# Revit family: Bath_Combination-GROHE-Concetto-19576_Series
name_source: partatom
category: Plumbing Fixtures
revit_build: Autodesk Revit 2014 (Build: 20130308_1515(x64)
units: mm (PartAtom-declared; Revit-internal decimal feet)

## types (2) — shared parameters
ADA Compliant = Yes
CW Connection = Yes
CWFU = 2
Cold Water Connection Diameter = 1/2"
Default Elevation = 0"
Description = Concetto Four-hole Single-lever Bath Combination
Flow Rate = 6.3 gpm (23.8 L/min), 2.5 gpm (9.5 L/min) for Hand Shower
HW Connection = Yes
HWFU = 3
Height = 12"
Hot Water Connection Diameter = 1"
Installation Type = Surface Mounted
Manufacturer = GROHE
Price = Prices may vary. Please consult Manufacturer Representative for most up-to-date price list.
Product Page URL = https://www.grohe.us
Tempered Water Connection Diameter = 1/2"
URL = https://www.grohe.us
Vent Connection = No
WFU = 4
Warranty Information = Limited Lifetime Warranty
Waste Connection = No
Width = 19 3/4"

## per-type parameters (varying)
| type | Assembly Code | Finish | Length | Material | Shipping Weight |
| 19576001 | D2020300 | Ceramic-Grohe-001-Starlight Chrome | 8 11/16" | Ceramic-Grohe-001-Starlight Chrome | 14.54 lb |
| 19576EN1 | D2020 | Ceramic-Grohe-EN1-Brushed Nickel | 9" | Ceramic-Grohe-EN1-Brushed Nickel | 16.39 lb |

note: column(s) folded — value = type name in every type: Model

## geometry (parser evidence)
native form markers: Sweep x1
no freeform markers — native parametric forms only
